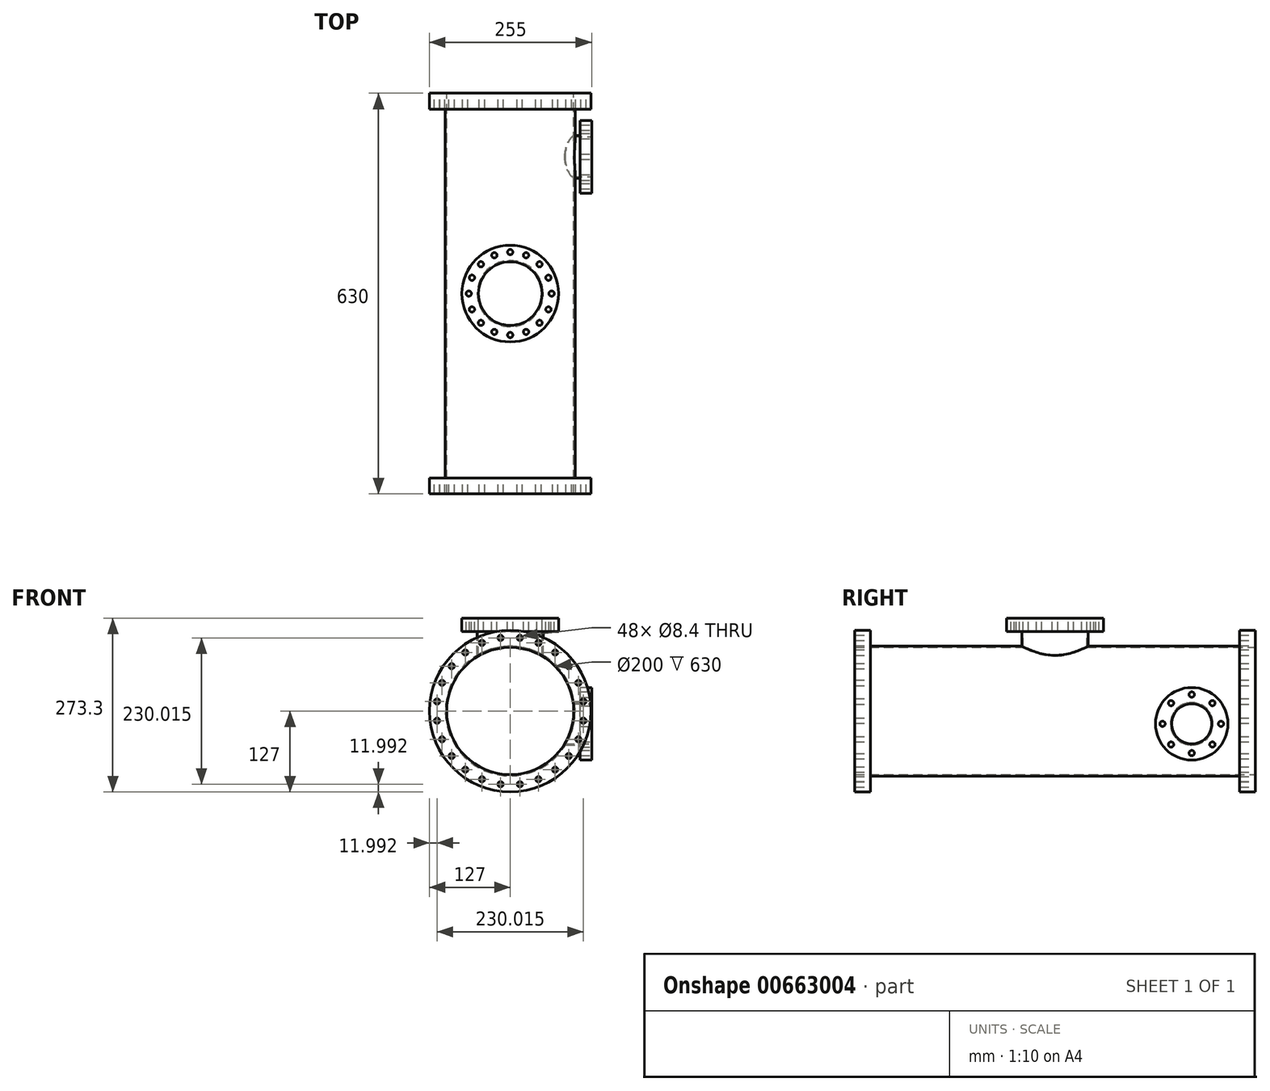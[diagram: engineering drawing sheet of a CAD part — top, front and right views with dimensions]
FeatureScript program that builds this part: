
annotation { "Feature Type Name" : "Feature", "Feature Type Description" : "" }
export const myFeature = defineFeature(function(context is Context, id is Id, definition is map)
    precondition{}
    {
        {
            var Q0;
            Q0=qCreatedBy(makeId("Front.planeOp"),FACE);
            var sketch = newSketch(context, id + "F0", { "sketchPlane" : qUnion([Q0])});
            skCircle(sketch, "E0", {"center": v(0, 0) * mm, "radius": 100 * mm});
            skCircle(sketch, "E1.0", {"center": v(0, 0) * mm, "radius": 102 * mm});
            skSolve(sketch);
        }
        {
            var Q0;
            Q0=makeQuery(id+"F0.imprint","IMPRINT",FACE,{"disambiguationData":[TD([[makeQuery(id+"F0.imprint","IMPRINT",EDGE,{"derivedFrom":sQuery(id+"F0.wireOp",EDGE,"E0")}),-1.0]])]});
            extrude(context, id + "F1", {"entities" : qUnion([Q0]), "depth" : (630 - 50) * mm, "offsetDistance" : 25 * mm});
        }
        {
            var Q0;
            Q0=makeQuery(id+"F1.opExtrude","CAP_FACE",FACE,{"disambiguationData":[OSD([sQuery(id+"F0.wireOp",EDGE,"E0"),sQuery(id+"F0.wireOp",EDGE,"E1.0")])],"isStart":false});
            var sketch = newSketch(context, id + "F2", { "sketchPlane" : qUnion([Q0])});
            skCircle(sketch, "E2", {"center": v(0, 0) * mm, "radius": 127 * mm});
            skSolve(sketch);
        }
        {
            var Q0;
            Q0=makeQuery(id+"F2.imprint","IMPRINT",FACE,{"disambiguationData":[TD([[makeQuery(id+"F2.imprint","IMPRINT",EDGE,{"derivedFrom":makeQuery(id+"F1.opExtrude","CAP_EDGE",EDGE,{"disambiguationData":[OSD([sQuery(id+"F0.wireOp",EDGE,"E0")])],"isStart":false})}),-1.0]])]});
            var Q1;
            Q1=makeQuery(id+"F2.imprint","IMPRINT",FACE,{"disambiguationData":[TD([[makeQuery(id+"F2.imprint","IMPRINT",EDGE,{"derivedFrom":sQuery(id+"F2.wireOp",EDGE,"E2")}),1.0]])]});
            extrude(context, id + "F3", {"entities" : qUnion([Q0, Q1]), "operationType" : NewBodyOperationType.ADD, "depth" : 25 * mm, "offsetDistance" : 25 * mm});
        }
        {
            var Q0;
            Q0=makeQuery(id+"F1.opExtrude","CAP_FACE",FACE,{"disambiguationData":[OSD([sQuery(id+"F0.wireOp",EDGE,"E0"),sQuery(id+"F0.wireOp",EDGE,"E1.0")])],"isStart":true});
            var sketch = newSketch(context, id + "F4", { "sketchPlane" : qUnion([Q0])});
            skCircle(sketch, "E3", {"center": v(0, 0) * mm, "radius": 127 * mm});
            skSolve(sketch);
        }
        {
            var Q0;
            Q0=makeQuery(id+"F4.imprint","IMPRINT",FACE,{"disambiguationData":[TD([[makeQuery(id+"F4.imprint","IMPRINT",EDGE,{"derivedFrom":makeQuery(id+"F1.opExtrude","CAP_EDGE",EDGE,{"disambiguationData":[OSD([sQuery(id+"F0.wireOp",EDGE,"E0")])],"isStart":true})}),1.0]])]});
            var Q1;
            Q1=makeQuery(id+"F4.imprint","IMPRINT",FACE,{"disambiguationData":[TD([[makeQuery(id+"F4.imprint","IMPRINT",EDGE,{"derivedFrom":sQuery(id+"F4.wireOp",EDGE,"E3")}),1.0]])]});
            extrude(context, id + "F5", {"entities" : qUnion([Q0, Q1]), "operationType" : NewBodyOperationType.ADD, "depth" : 25 * mm, "offsetDistance" : 25 * mm});
        }
        {
            var Q0;
            Q0=makeQuery(id+"F5.opExtrude","CAP_FACE",FACE,{"disambiguationData":[OSD([sQuery(id+"F0.wireOp",EDGE,"E0"),sQuery(id+"F4.wireOp",EDGE,"E3")])],"isStart":false});
            var sketch = newSketch(context, id + "F6", { "sketchPlane" : qUnion([Q0])});
            skCircle(sketch, "E4", {"center": v(0, 0) * mm, "radius": 116 * mm, "construction": true});
            skPoint(sketch, "E5", {"position": v(15.14, 115) * mm});
            skLineSegment(sketch, "E6", {"start": v(0, 0) * mm, "end": v(15.14, 115) * mm, "construction": true});
            skPoint(sketch, "E7.1.0", {"position": v(-15.14, 115) * mm});
            skPoint(sketch, "E7.2.0", {"position": v(-44.4, 107.17) * mm});
            skPoint(sketch, "E7.3.0", {"position": v(-70.62, 92.03) * mm});
            skPoint(sketch, "E7.4.0", {"position": v(-92.03, 70.62) * mm});
            skPoint(sketch, "E7.5.0", {"position": v(-107.17, 44.4) * mm});
            skPoint(sketch, "E7.6.0", {"position": v(-115, 15.14) * mm});
            skPoint(sketch, "E7.7.0", {"position": v(-115, -15.14) * mm});
            skPoint(sketch, "E7.8.0", {"position": v(-107.17, -44.4) * mm});
            skPoint(sketch, "E7.9.0", {"position": v(-92.03, -70.62) * mm});
            skPoint(sketch, "E7.10.0", {"position": v(-70.62, -92.03) * mm});
            skPoint(sketch, "E7.11.0", {"position": v(-44.4, -107.17) * mm});
            skPoint(sketch, "E7.12.0", {"position": v(-15.14, -115) * mm});
            skPoint(sketch, "E7.13.0", {"position": v(15.14, -115) * mm});
            skPoint(sketch, "E7.14.0", {"position": v(44.4, -107.17) * mm});
            skPoint(sketch, "E7.15.0", {"position": v(70.62, -92.03) * mm});
            skPoint(sketch, "E7.16.0", {"position": v(92.03, -70.62) * mm});
            skPoint(sketch, "E7.17.0", {"position": v(107.17, -44.4) * mm});
            skPoint(sketch, "E7.18.0", {"position": v(115, -15.14) * mm});
            skPoint(sketch, "E7.19.0", {"position": v(115, 15.14) * mm});
            skPoint(sketch, "E7.20.0", {"position": v(107.17, 44.4) * mm});
            skPoint(sketch, "E7.21.0", {"position": v(92.03, 70.62) * mm});
            skPoint(sketch, "E7.22.0", {"position": v(70.62, 92.03) * mm});
            skPoint(sketch, "E7.23.0", {"position": v(44.4, 107.17) * mm});
            skSolve(sketch);
        }
        {
            var Q0;
            Q0=sQuery(id+"F6.wireOp",VERTEX,"E5");
            var Q1;
            Q1=sQuery(id+"F6.wireOp",VERTEX,"E7.23.0");
            var Q2;
            Q2=sQuery(id+"F6.wireOp",VERTEX,"E7.22.0");
            var Q3;
            Q3=sQuery(id+"F6.wireOp",VERTEX,"E7.21.0");
            var Q4;
            Q4=sQuery(id+"F6.wireOp",VERTEX,"E7.20.0");
            var Q5;
            Q5=sQuery(id+"F6.wireOp",VERTEX,"E7.19.0");
            var Q6;
            Q6=sQuery(id+"F6.wireOp",VERTEX,"E7.18.0");
            var Q7;
            Q7=sQuery(id+"F6.wireOp",VERTEX,"E7.17.0");
            var Q8;
            Q8=sQuery(id+"F6.wireOp",VERTEX,"E7.16.0");
            var Q9;
            Q9=sQuery(id+"F6.wireOp",VERTEX,"E7.15.0");
            var Q10;
            Q10=sQuery(id+"F6.wireOp",VERTEX,"E7.14.0");
            var Q11;
            Q11=sQuery(id+"F6.wireOp",VERTEX,"E7.13.0");
            var Q12;
            Q12=sQuery(id+"F6.wireOp",VERTEX,"E7.12.0");
            var Q13;
            Q13=sQuery(id+"F6.wireOp",VERTEX,"E7.11.0");
            var Q14;
            Q14=sQuery(id+"F6.wireOp",VERTEX,"E7.10.0");
            var Q15;
            Q15=sQuery(id+"F6.wireOp",VERTEX,"E7.9.0");
            var Q16;
            Q16=sQuery(id+"F6.wireOp",VERTEX,"E7.8.0");
            var Q17;
            Q17=sQuery(id+"F6.wireOp",VERTEX,"E7.7.0");
            var Q18;
            Q18=sQuery(id+"F6.wireOp",VERTEX,"E7.6.0");
            var Q19;
            Q19=sQuery(id+"F6.wireOp",VERTEX,"E7.5.0");
            var Q20;
            Q20=sQuery(id+"F6.wireOp",VERTEX,"E7.4.0");
            var Q21;
            Q21=sQuery(id+"F6.wireOp",VERTEX,"E7.3.0");
            var Q22;
            Q22=sQuery(id+"F6.wireOp",VERTEX,"E7.2.0");
            var Q23;
            Q23=sQuery(id+"F6.wireOp",VERTEX,"E7.1.0");
            var Q24;
            Q24=makeQuery(id+"F1.opExtrude","SWEPT_BODY",BODY,{"disambiguationData":[OSD([sQuery(id+"F0.wireOp",EDGE,"E0"),sQuery(id+"F0.wireOp",EDGE,"E1.0")])]});
            hole(context, id + "F7", {"style" : HoleStyle.SIMPLE, "endStyle" : HoleEndStyle.THROUGH, "standardTappedOrClearance" : lookupTablePath({ "fit" : "Close", "standard" : "ISO", "size" : "M8", "type" : "Clearance" }), "standardBlindInLast" : lookupTablePath({ "fit" : "Close", "standard" : "ISO", "engagement" : "75%", "pitch" : "1.25 mm", "size" : "M8", "type" : "Clearance & tapped" }), "holeDiameter" : 8.4 * mm, "majorDiameter" : 5 * mm, "isTappedThrough" : true, "tappedDepth" : 12 * mm, "tapClearance" : 3, "locations" : qUnion([Q0, Q1, Q2, Q3, Q4, Q5, Q6, Q7, Q8, Q9, Q10, Q11, Q12, Q13, Q14, Q15, Q16, Q17, Q18, Q19, Q20, Q21, Q22, Q23]), "scope" : qUnion([Q24])});
        }
        {
            var Q0;
            Q0=qCreatedBy(makeId("Top.planeOp"),FACE);
            cPlane(context, id + "F8", {"entities" : qUnion([Q0]), "cplaneType" : CPlaneType.OFFSET, "offset" : 125 * mm, "width" : 150 * mm, "height" : 150 * mm});
        }
        {
            var Q0;
            Q0=qCreatedBy(id+"F8.planeOp",FACE);
            var sketch = newSketch(context, id + "F9", { "sketchPlane" : qUnion([Q0])});
            skCircle(sketch, "E8", {"center": v(0, -290) * mm, "radius": 50 * mm});
            skLineSegment(sketch, "E9", {"start": v(0, -290) * mm, "end": v(0, 0) * mm, "construction": true});
            skLineSegment(sketch, "E10", {"start": v(0, 0) * mm, "end": v(0, -290) * mm, "construction": true});
            skLineSegment(sketch, "E11", {"start": v(0, -580) * mm, "end": v(0, -290) * mm, "construction": true});
            skCircle(sketch, "E12.0", {"center": v(0, -290) * mm, "radius": 52 * mm});
            skCircle(sketch, "E13", {"center": v(0, -290) * mm, "radius": 76 * mm});
            skSolve(sketch);
        }
        {
            var Q0;
            Q0=makeQuery(id+"F9.imprint","IMPRINT",FACE,{"disambiguationData":[TD([[makeQuery(id+"F9.imprint","IMPRINT",EDGE,{"derivedFrom":sQuery(id+"F9.wireOp",EDGE,"E8")}),-1.0]])]});
            var Q1;
            Q1=makeQuery(id+"F1.opExtrude","SWEPT_FACE",FACE,{"disambiguationData":[OSD([sQuery(id+"F0.wireOp",EDGE,"E1.0")])]});
            extrude(context, id + "F10", {"entities" : qUnion([Q0]), "operationType" : NewBodyOperationType.ADD, "endBound" : BoundingType.UP_TO_SURFACE, "oppositeDirection" : true, "depth" : 25 * mm, "endBoundEntityFace" : qUnion([Q1]), "offsetDistance" : 25 * mm});
        }
        {
            var Q0;
            Q0=makeQuery(id+"F9.imprint","IMPRINT",FACE,{"disambiguationData":[TD([[makeQuery(id+"F9.imprint","IMPRINT",EDGE,{"derivedFrom":sQuery(id+"F9.wireOp",EDGE,"E8")}),1.0]])]});
            var Q1;
            {var subQ0=sQuery(id+"F0.wireOp",EDGE,"E0");Q1=makeQuery(id+"F5.boolean.opBoolean","MERGE",FACE,{"derivedFrom":[makeQuery(id+"F3.boolean.opBoolean","MERGE",FACE,{"derivedFrom":[makeQuery(id+"F1.opExtrude","SWEPT_FACE",FACE,{"disambiguationData":[OSD([subQ0])]}),makeQuery(id+"F3.opExtrude","SWEPT_FACE",FACE,{"disambiguationData":[OSD([subQ0])]})]}),makeQuery(id+"F5.opExtrude","SWEPT_FACE",FACE,{"disambiguationData":[OSD([subQ0])]})]});}
            extrude(context, id + "F11", {"entities" : qUnion([Q0]), "operationType" : NewBodyOperationType.REMOVE, "endBound" : BoundingType.UP_TO_SURFACE, "oppositeDirection" : true, "depth" : 25 * mm, "endBoundEntityFace" : qUnion([Q1]), "offsetDistance" : 25 * mm});
        }
        {
            var Q0;
            Q0=makeQuery(id+"F9.imprint","IMPRINT",FACE,{"disambiguationData":[TD([[makeQuery(id+"F9.imprint","IMPRINT",EDGE,{"derivedFrom":sQuery(id+"F9.wireOp",EDGE,"E8")}),-1.0]])]});
            var Q1;
            Q1=makeQuery(id+"F9.imprint","IMPRINT",FACE,{"disambiguationData":[TD([[makeQuery(id+"F9.imprint","IMPRINT",EDGE,{"derivedFrom":sQuery(id+"F9.wireOp",EDGE,"E12.0")}),-1.0]])]});
            extrude(context, id + "F12", {"entities" : qUnion([Q0, Q1]), "operationType" : NewBodyOperationType.ADD, "depth" : 21.3 * mm, "offsetDistance" : 25 * mm});
        }
        {
            var Q0;
            Q0=makeQuery(id+"F12.opExtrude","CAP_FACE",FACE,{"disambiguationData":[OSD([sQuery(id+"F9.wireOp",EDGE,"E8"),sQuery(id+"F9.wireOp",EDGE,"E13")])],"isStart":false});
            var sketch = newSketch(context, id + "F13", { "sketchPlane" : qUnion([Q0])});
            skCircle(sketch, "E14", {"center": v(0, -290) * mm, "radius": 65.15 * mm, "construction": true});
            skPoint(sketch, "E15", {"position": v(0, -224.85) * mm});
            skPoint(sketch, "E16.1.0", {"position": v(-24.93, -229.8) * mm});
            skPoint(sketch, "E16.2.0", {"position": v(-46.07, -243.93) * mm});
            skPoint(sketch, "E16.3.0", {"position": v(-60.2, -265.07) * mm});
            skPoint(sketch, "E16.4.0", {"position": v(-65.15, -290) * mm});
            skPoint(sketch, "E16.5.0", {"position": v(-60.2, -314.93) * mm});
            skPoint(sketch, "E16.6.0", {"position": v(-46.07, -336.07) * mm});
            skPoint(sketch, "E16.7.0", {"position": v(-24.93, -350.2) * mm});
            skPoint(sketch, "E16.8.0", {"position": v(0, -355.15) * mm});
            skPoint(sketch, "E16.9.0", {"position": v(24.93, -350.2) * mm});
            skPoint(sketch, "E16.10.0", {"position": v(46.07, -336.07) * mm});
            skPoint(sketch, "E16.11.0", {"position": v(60.2, -314.93) * mm});
            skPoint(sketch, "E16.12.0", {"position": v(65.15, -290) * mm});
            skPoint(sketch, "E16.13.0", {"position": v(60.2, -265.07) * mm});
            skPoint(sketch, "E16.14.0", {"position": v(46.07, -243.93) * mm});
            skPoint(sketch, "E16.15.0", {"position": v(24.93, -229.8) * mm});
            skSolve(sketch);
        }
        {
            var Q0;
            Q0=sQuery(id+"F13.wireOp",VERTEX,"E15");
            var Q1;
            Q1=sQuery(id+"F13.wireOp",VERTEX,"E16.15.0");
            var Q2;
            Q2=sQuery(id+"F13.wireOp",VERTEX,"E16.14.0");
            var Q3;
            Q3=sQuery(id+"F13.wireOp",VERTEX,"E16.13.0");
            var Q4;
            Q4=sQuery(id+"F13.wireOp",VERTEX,"E16.12.0");
            var Q5;
            Q5=sQuery(id+"F13.wireOp",VERTEX,"E16.11.0");
            var Q6;
            Q6=sQuery(id+"F13.wireOp",VERTEX,"E16.10.0");
            var Q7;
            Q7=sQuery(id+"F13.wireOp",VERTEX,"E16.9.0");
            var Q8;
            Q8=sQuery(id+"F13.wireOp",VERTEX,"E16.8.0");
            var Q9;
            Q9=sQuery(id+"F13.wireOp",VERTEX,"E16.7.0");
            var Q10;
            Q10=sQuery(id+"F13.wireOp",VERTEX,"E16.6.0");
            var Q11;
            Q11=sQuery(id+"F13.wireOp",VERTEX,"E16.5.0");
            var Q12;
            Q12=sQuery(id+"F13.wireOp",VERTEX,"E16.4.0");
            var Q13;
            Q13=sQuery(id+"F13.wireOp",VERTEX,"E16.3.0");
            var Q14;
            Q14=sQuery(id+"F13.wireOp",VERTEX,"E16.2.0");
            var Q15;
            Q15=sQuery(id+"F13.wireOp",VERTEX,"E16.1.0");
            var Q16;
            Q16=makeQuery(id+"F1.opExtrude","SWEPT_BODY",BODY,{"disambiguationData":[OSD([sQuery(id+"F0.wireOp",EDGE,"E0"),sQuery(id+"F0.wireOp",EDGE,"E1.0")])]});
            hole(context, id + "F14", {"style" : HoleStyle.SIMPLE, "endStyle" : HoleEndStyle.BLIND, "standardTappedOrClearance" : lookupTablePath({ "fit" : "Close", "standard" : "ISO", "size" : "M8", "type" : "Clearance" }), "standardBlindInLast" : lookupTablePath({ "fit" : "Close", "standard" : "ISO", "engagement" : "75%", "pitch" : "1.25 mm", "size" : "M8", "type" : "Clearance & tapped" }), "holeDiameter" : 8.4 * mm, "majorDiameter" : 5 * mm, "holeDepth" : 27 * mm, "isTappedThrough" : true, "tappedDepth" : 12 * mm, "tapClearance" : 3, "locations" : qUnion([Q0, Q1, Q2, Q3, Q4, Q5, Q6, Q7, Q8, Q9, Q10, Q11, Q12, Q13, Q14, Q15]), "scope" : qUnion([Q16])});
        }
        {
            var Q0;
            Q0=qCreatedBy(makeId("Right.planeOp"),FACE);
            cPlane(context, id + "F15", {"entities" : qUnion([Q0]), "cplaneType" : CPlaneType.OFFSET, "offset" : 110 * mm, "width" : 150 * mm, "height" : 150 * mm});
        }
        {
            var Q0;
            Q0=qCreatedBy(id+"F15.planeOp",FACE);
            var sketch = newSketch(context, id + "F16", { "sketchPlane" : qUnion([Q0])});
            skCircle(sketch, "E17", {"center": v(-75, -20) * mm, "radius": 31.5 * mm});
            skCircle(sketch, "E18.0", {"center": v(-75, -20) * mm, "radius": 33.5 * mm});
            skCircle(sketch, "E19", {"center": v(-75, -20) * mm, "radius": 57 * mm});
            skSolve(sketch);
        }
        {
            var Q0;
            Q0=makeQuery(id+"F16.imprint","IMPRINT",FACE,{"disambiguationData":[TD([[makeQuery(id+"F16.imprint","IMPRINT",EDGE,{"derivedFrom":sQuery(id+"F16.wireOp",EDGE,"E17")}),-1.0]])]});
            var Q1;
            Q1=makeQuery(id+"F10.boolean.opBoolean","SPLIT",FACE,{"disambiguationData":[TD([makeQuery(id+"F10.opExtrude","SWEPT_FACE",FACE,{"disambiguationData":[OSD([sQuery(id+"F9.wireOp",EDGE,"E12.0")])]})])],"derivedFrom":makeQuery(id+"F1.opExtrude","SWEPT_FACE",FACE,{"disambiguationData":[OSD([sQuery(id+"F0.wireOp",EDGE,"E1.0")])]})});
            extrude(context, id + "F17", {"entities" : qUnion([Q0]), "operationType" : NewBodyOperationType.ADD, "endBound" : BoundingType.UP_TO_SURFACE, "oppositeDirection" : true, "depth" : 25 * mm, "endBoundEntityFace" : qUnion([Q1]), "offsetDistance" : 25 * mm});
        }
        {
            var Q0;
            Q0=makeQuery(id+"F16.imprint","IMPRINT",FACE,{"disambiguationData":[TD([[makeQuery(id+"F16.imprint","IMPRINT",EDGE,{"derivedFrom":sQuery(id+"F16.wireOp",EDGE,"E17")}),1.0]])]});
            var Q1;
            {var subQ0=sQuery(id+"F0.wireOp",EDGE,"E0");Q1=makeQuery(id+"F5.boolean.opBoolean","MERGE",FACE,{"derivedFrom":[makeQuery(id+"F3.boolean.opBoolean","MERGE",FACE,{"derivedFrom":[makeQuery(id+"F1.opExtrude","SWEPT_FACE",FACE,{"disambiguationData":[OSD([subQ0])]}),makeQuery(id+"F3.opExtrude","SWEPT_FACE",FACE,{"disambiguationData":[OSD([subQ0])]})]}),makeQuery(id+"F5.opExtrude","SWEPT_FACE",FACE,{"disambiguationData":[OSD([subQ0])]})]});}
            extrude(context, id + "F18", {"entities" : qUnion([Q0]), "operationType" : NewBodyOperationType.REMOVE, "endBound" : BoundingType.UP_TO_SURFACE, "oppositeDirection" : true, "depth" : 25 * mm, "endBoundEntityFace" : qUnion([Q1]), "offsetDistance" : 25 * mm});
        }
        {
            var Q0;
            Q0=makeQuery(id+"F16.imprint","IMPRINT",FACE,{"disambiguationData":[TD([[makeQuery(id+"F16.imprint","IMPRINT",EDGE,{"derivedFrom":sQuery(id+"F16.wireOp",EDGE,"E17")}),-1.0]])]});
            var Q1;
            Q1=makeQuery(id+"F16.imprint","IMPRINT",FACE,{"disambiguationData":[TD([[makeQuery(id+"F16.imprint","IMPRINT",EDGE,{"derivedFrom":sQuery(id+"F16.wireOp",EDGE,"E18.0")}),-1.0]])]});
            extrude(context, id + "F19", {"entities" : qUnion([Q0, Q1]), "operationType" : NewBodyOperationType.ADD, "depth" : 18 * mm, "offsetDistance" : 25 * mm});
        }
        {
            var Q0;
            Q0=makeQuery(id+"F19.opExtrude","CAP_FACE",FACE,{"disambiguationData":[OSD([sQuery(id+"F16.wireOp",EDGE,"E17"),sQuery(id+"F16.wireOp",EDGE,"E19")])],"isStart":false});
            var sketch = newSketch(context, id + "F20", { "sketchPlane" : qUnion([Q0])});
            skCircle(sketch, "E20", {"center": v(-75, -20) * mm, "radius": 46 * mm, "construction": true});
            skPoint(sketch, "E21", {"position": v(-75, 26) * mm});
            skLineSegment(sketch, "E22", {"start": v(-75, 26) * mm, "end": v(-75, -20) * mm, "construction": true});
            skPoint(sketch, "E23.1.0", {"position": v(-107.53, 12.53) * mm});
            skPoint(sketch, "E23.2.0", {"position": v(-121, -20) * mm});
            skPoint(sketch, "E23.3.0", {"position": v(-107.53, -52.53) * mm});
            skPoint(sketch, "E23.4.0", {"position": v(-75, -66) * mm});
            skPoint(sketch, "E23.5.0", {"position": v(-42.47, -52.53) * mm});
            skPoint(sketch, "E23.6.0", {"position": v(-29, -20) * mm});
            skPoint(sketch, "E23.7.0", {"position": v(-42.47, 12.53) * mm});
            skSolve(sketch);
        }
        {
            var Q0;
            Q0=sQuery(id+"F20.wireOp",VERTEX,"E21");
            var Q1;
            Q1=sQuery(id+"F20.wireOp",VERTEX,"E23.7.0");
            var Q2;
            Q2=sQuery(id+"F20.wireOp",VERTEX,"E23.6.0");
            var Q3;
            Q3=sQuery(id+"F20.wireOp",VERTEX,"E23.5.0");
            var Q4;
            Q4=sQuery(id+"F20.wireOp",VERTEX,"E23.4.0");
            var Q5;
            Q5=sQuery(id+"F20.wireOp",VERTEX,"E23.3.0");
            var Q6;
            Q6=sQuery(id+"F20.wireOp",VERTEX,"E23.2.0");
            var Q7;
            Q7=sQuery(id+"F20.wireOp",VERTEX,"E23.1.0");
            var Q8;
            Q8=makeQuery(id+"F1.opExtrude","SWEPT_BODY",BODY,{"disambiguationData":[OSD([sQuery(id+"F0.wireOp",EDGE,"E0"),sQuery(id+"F0.wireOp",EDGE,"E1.0")])]});
            hole(context, id + "F21", {"style" : HoleStyle.SIMPLE, "endStyle" : HoleEndStyle.BLIND, "standardTappedOrClearance" : lookupTablePath({ "fit" : "Close", "standard" : "ISO", "size" : "M8", "type" : "Clearance" }), "standardBlindInLast" : lookupTablePath({ "fit" : "Close", "standard" : "ISO", "engagement" : "75%", "pitch" : "1.25 mm", "size" : "M8", "type" : "Clearance & tapped" }), "holeDiameter" : 8.4 * mm, "majorDiameter" : 5 * mm, "holeDepth" : 24 * mm, "isTappedThrough" : true, "tappedDepth" : 12 * mm, "tapClearance" : 3, "locations" : qUnion([Q0, Q1, Q2, Q3, Q4, Q5, Q6, Q7]), "scope" : qUnion([Q8])});
        }
    });
